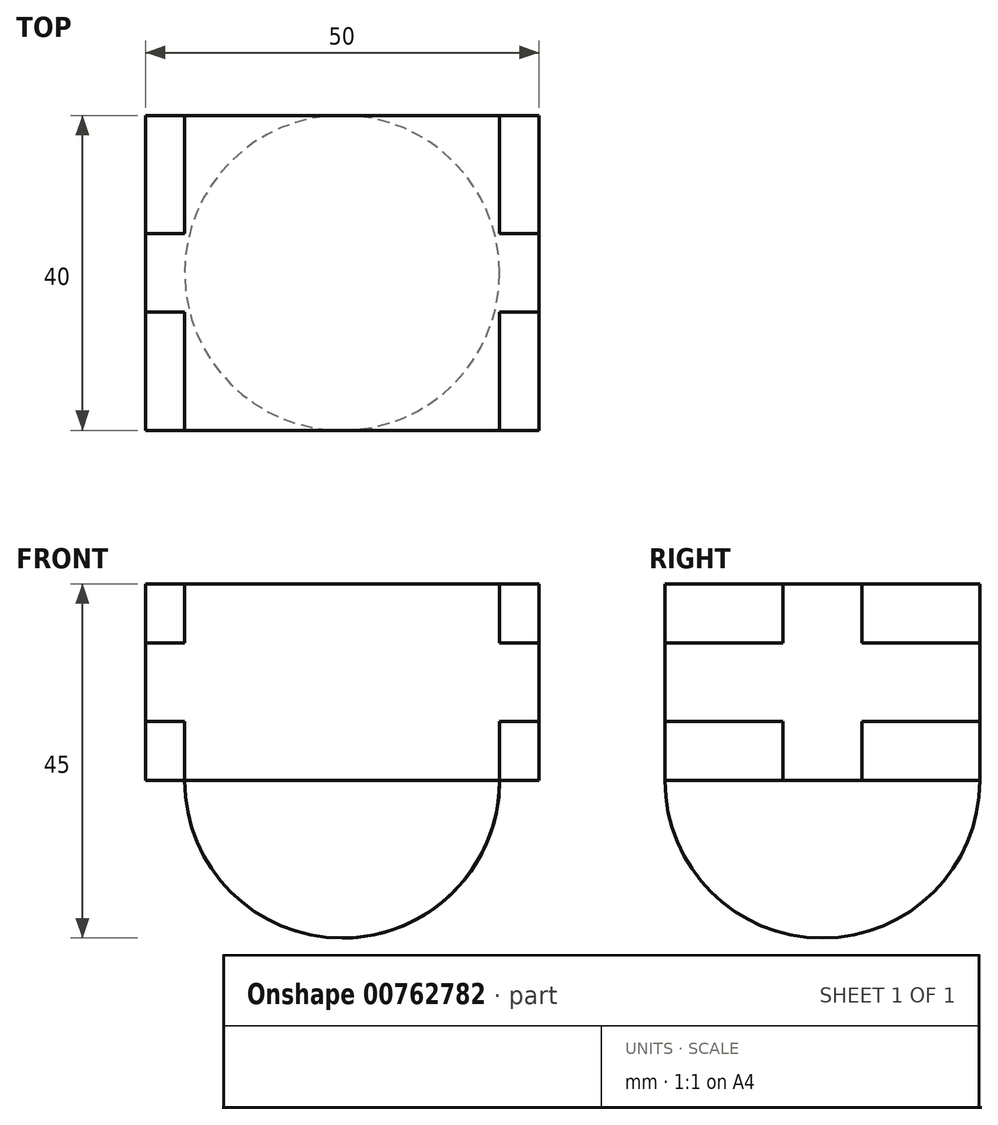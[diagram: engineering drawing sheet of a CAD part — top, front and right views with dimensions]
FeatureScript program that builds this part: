
annotation { "Feature Type Name" : "Feature", "Feature Type Description" : "" }
export const myFeature = defineFeature(function(context is Context, id is Id, definition is map)
    precondition{}
    {
        {
            var Q0;
            Q0=qCreatedBy(makeId("Front.planeOp"),FACE);
            var sketch = newSketch(context, id + "F0", { "sketchPlane" : qUnion([Q0])});
            skLineSegment(sketch, "E0.bottom", {"start": v(20, -20) * mm, "end": v(-20, -20) * mm});
            skLineSegment(sketch, "E0.top", {"start": v(20, 20) * mm, "end": v(-20, 20) * mm});
            skLineSegment(sketch, "E0.left", {"start": v(20, -20) * mm, "end": v(20, 20) * mm});
            skLineSegment(sketch, "E0.right", {"start": v(-20, -20) * mm, "end": v(-20, 20) * mm});
            skPoint(sketch, "E0.middle", {"position": v(0, 0) * mm});
            skSolve(sketch);
        }
        {
            var Q0;
            Q0 = qSketchRegion(id + "F0", true);
            extrude(context, id + "F1", {"entities" : qUnion([Q0]), "depth" : 40 * mm, "offsetDistance" : 25 * mm});
        }
        {
            var Q0;
            Q0=makeQuery(id+"F1.opExtrude","SWEPT_FACE",FACE,{"disambiguationData":[OSD([sQuery(id+"F0.wireOp",EDGE,"E0.top")])]});
            var Q1;
            Q1=makeQuery(id+"F1.opExtrude","CAP_FACE",FACE,{"disambiguationData":[OSD([sQuery(id+"F0.wireOp",EDGE,"E0.bottom"),sQuery(id+"F0.wireOp",EDGE,"E0.top"),sQuery(id+"F0.wireOp",EDGE,"E0.left"),sQuery(id+"F0.wireOp",EDGE,"E0.right")])],"isStart":false});
            var Q2;
            Q2=makeQuery(id+"F1.opExtrude","SWEPT_FACE",FACE,{"disambiguationData":[OSD([sQuery(id+"F0.wireOp",EDGE,"E0.left")])]});
            var Q3;
            Q3=makeQuery(id+"F1.opExtrude","CAP_FACE",FACE,{"disambiguationData":[OSD([sQuery(id+"F0.wireOp",EDGE,"E0.bottom"),sQuery(id+"F0.wireOp",EDGE,"E0.top"),sQuery(id+"F0.wireOp",EDGE,"E0.left"),sQuery(id+"F0.wireOp",EDGE,"E0.right")])],"isStart":true});
            var Q4;
            Q4=makeQuery(id+"F1.opExtrude","SWEPT_FACE",FACE,{"disambiguationData":[OSD([sQuery(id+"F0.wireOp",EDGE,"E0.right")])]});
            var Q5;
            Q5=makeQuery(id+"F1.opExtrude","SWEPT_FACE",FACE,{"disambiguationData":[OSD([sQuery(id+"F0.wireOp",EDGE,"E0.bottom")])]});
            fillet(context, id + "F2", {"entities" : qUnion([Q0, Q1, Q2, Q3, Q4, Q5]), "radius" : 20 * mm, "tangentPropagation" : true, "allowEdgeOverflow" : false});
        }
        {
            var Q0;
            Q0=qCreatedBy(makeId("Top.planeOp"),FACE);
            var sketch = newSketch(context, id + "F3", { "sketchPlane" : qUnion([Q0])});
            skPoint(sketch, "E1.startSnap0", {"position": v(0, -20) * mm});
            skLineSegment(sketch, "E2.bottom", {"start": v(20, 0) * mm, "end": v(-20, 0) * mm});
            skLineSegment(sketch, "E2.top", {"start": v(20, -40) * mm, "end": v(-20, -40) * mm});
            skLineSegment(sketch, "E2.left", {"start": v(20, 0) * mm, "end": v(20, -40) * mm});
            skLineSegment(sketch, "E2.right", {"start": v(-20, 0) * mm, "end": v(-20, -40) * mm});
            skSolve(sketch);
        }
        {
            var Q0;
            Q0 = qSketchRegion(id + "F3", true);
            extrude(context, id + "F4", {"entities" : qUnion([Q0]), "operationType" : NewBodyOperationType.ADD, "depth" : 25 * mm, "offsetDistance" : 25 * mm});
        }
        {
            var Q0;
            Q0=qCreatedBy(makeId("Right.planeOp"),FACE);
            var sketch = newSketch(context, id + "F5", { "sketchPlane" : qUnion([Q0])});
            skPoint(sketch, "E3.startSnap0", {"position": v(-20, 12.5) * mm});
            skLineSegment(sketch, "E4", {"start": v(-20, 0) * mm, "end": v(-25, 0) * mm});
            skLineSegment(sketch, "E5", {"start": v(-20, 0) * mm, "end": v(-15, 0) * mm});
            skLineSegment(sketch, "E6", {"start": v(-25, 25) * mm, "end": v(-25, 17.5) * mm});
            skLineSegment(sketch, "E7", {"start": v(-40, 17.5) * mm, "end": v(-25, 17.5) * mm});
            skLineSegment(sketch, "E8", {"start": v(-40, 7.5) * mm, "end": v(-25, 7.5) * mm});
            skLineSegment(sketch, "E9", {"start": v(-15, 25) * mm, "end": v(-15, 17.5) * mm});
            skLineSegment(sketch, "E10", {"start": v(-40, 17.5) * mm, "end": v(-40, 7.5) * mm});
            skLineSegment(sketch, "E11", {"start": v(-25, 25) * mm, "end": v(-15, 25) * mm});
            skLineSegment(sketch, "E12", {"start": v(0, 17.5) * mm, "end": v(0, 7.5) * mm});
            skLineSegment(sketch, "E13", {"start": v(-25, 0) * mm, "end": v(-15, 0) * mm});
            skLineSegment(sketch, "E14.trimOffspring", {"start": v(-25, 7.5) * mm, "end": v(-25, 0) * mm});
            skLineSegment(sketch, "E15.trimOffspring", {"start": v(-15, 7.5) * mm, "end": v(-15, 0) * mm});
            skLineSegment(sketch, "E16.trimOffspring", {"start": v(-15, 17.5) * mm, "end": v(0, 17.5) * mm});
            skLineSegment(sketch, "E17.trimOffspring", {"start": v(-15, 7.5) * mm, "end": v(0, 7.5) * mm});
            skSolve(sketch);
        }
        {
            var Q0;
            Q0 = qSketchRegion(id + "F5", true);
            extrude(context, id + "F6", {"entities" : qUnion([Q0]), "operationType" : NewBodyOperationType.ADD, "depth" : 25 * mm, "offsetDistance" : 25 * mm});
        }
        {
            var Q0;
            Q0=makeQuery(id+"F6.opExtrude","CAP_FACE",FACE,{"disambiguationData":[OSD([sQuery(id+"F5.wireOp",EDGE,"E6"),sQuery(id+"F5.wireOp",EDGE,"E7"),sQuery(id+"F5.wireOp",EDGE,"E8"),sQuery(id+"F5.wireOp",EDGE,"E9"),sQuery(id+"F5.wireOp",EDGE,"E10"),sQuery(id+"F5.wireOp",EDGE,"E11"),sQuery(id+"F5.wireOp",EDGE,"E12"),sQuery(id+"F5.wireOp",EDGE,"E13"),sQuery(id+"F5.wireOp",EDGE,"E14.trimOffspring"),sQuery(id+"F5.wireOp",EDGE,"E15.trimOffspring"),sQuery(id+"F5.wireOp",EDGE,"E16.trimOffspring"),sQuery(id+"F5.wireOp",EDGE,"E17.trimOffspring")])],"isStart":false});
            extrude(context, id + "F7", {"entities" : qUnion([Q0]), "operationType" : NewBodyOperationType.ADD, "oppositeDirection" : true, "depth" : 50 * mm, "offsetDistance" : 25 * mm});
        }
    });
